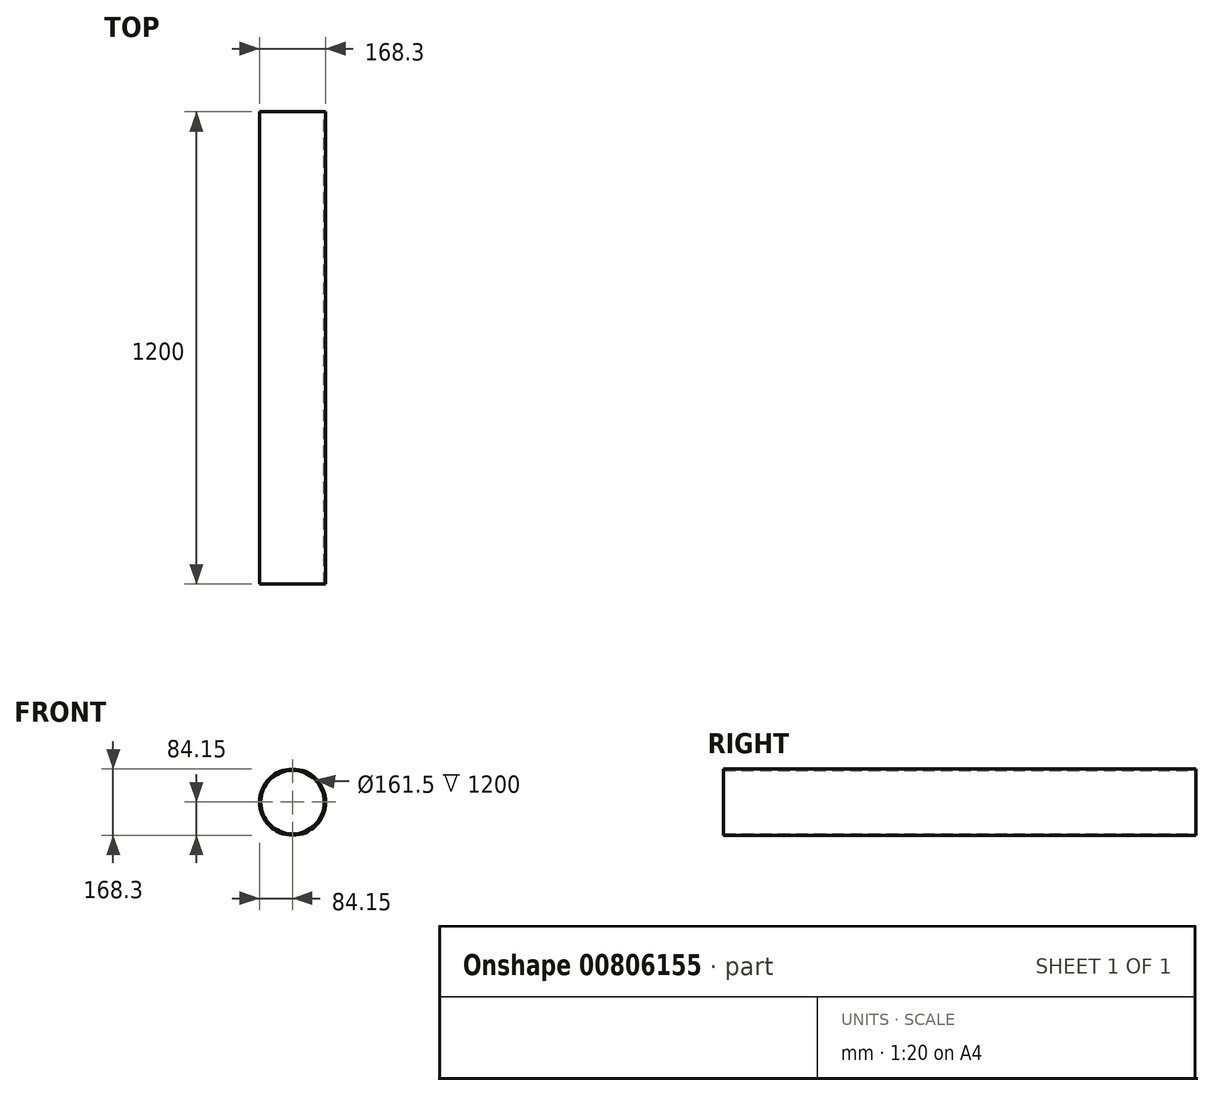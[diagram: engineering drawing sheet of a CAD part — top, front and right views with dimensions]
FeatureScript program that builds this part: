
annotation { "Feature Type Name" : "Feature", "Feature Type Description" : "" }
export const myFeature = defineFeature(function(context is Context, id is Id, definition is map)
    precondition{}
    {
        {
            var Q0;
            Q0=qCreatedBy(makeId("Front.planeOp"),FACE);
            var sketch = newSketch(context, id + "F0", { "sketchPlane" : qUnion([Q0])});
            skCircle(sketch, "E0", {"center": v(0, 0) * mm, "radius": 80.75 * mm});
            skCircle(sketch, "E1", {"center": v(0, 0) * mm, "radius": 84.15 * mm});
            skSolve(sketch);
        }
        {
            var Q0;
            Q0=qSketchRegion(id+"F0",true);
            extrude(context, id + "F1", {"entities" : qUnion([Q0]), "depth" : 1200 * mm, "offsetDistance" : 25 * mm});
        }
    });
